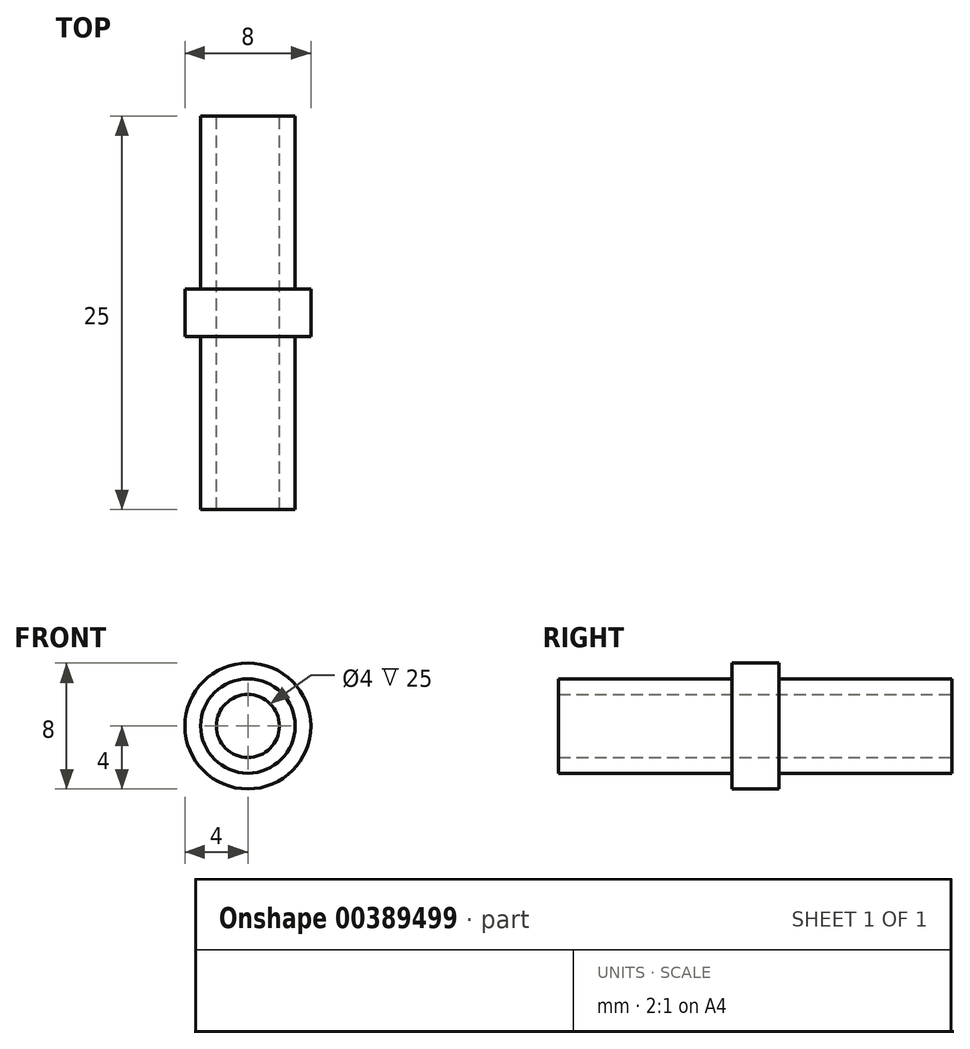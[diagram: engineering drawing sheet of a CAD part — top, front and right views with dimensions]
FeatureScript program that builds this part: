
annotation { "Feature Type Name" : "Feature", "Feature Type Description" : "" }
export const myFeature = defineFeature(function(context is Context, id is Id, definition is map)
    precondition{}
    {
        {
            var Q0;
            Q0=qCreatedBy(makeId("Front.planeOp"),FACE);
            var sketch = newSketch(context, id + "F0", { "sketchPlane" : qUnion([Q0])});
            skCircle(sketch, "E0", {"center": v(0, 0) * mm, "radius": 4 * mm});
            skSolve(sketch);
        }
        {
            var Q0;
            Q0=qCreatedBy(makeId("Front.planeOp"),FACE);
            var sketch = newSketch(context, id + "F1", { "sketchPlane" : qUnion([Q0])});
            skCircle(sketch, "E1", {"center": v(0, 0) * mm, "radius": 3 * mm});
            skSolve(sketch);
        }
        {
            var Q0;
            Q0=qSketchRegion(id+"F1",true);
            extrude(context, id + "F2", {"entities" : qUnion([Q0]), "depth" : 25 * mm});
        }
        {
            var Q0;
            Q0=qSketchRegion(id+"F0",true);
            extrude(context, id + "F3", {"entities" : qUnion([Q0]), "operationType" : NewBodyOperationType.ADD, "depth" : 14 * mm});
        }
        {
            var Q0;
            Q0=makeQuery(id+"F3.boolean.opBoolean","MERGE",FACE,{"derivedFrom":[makeQuery(id+"F2.opExtrude","CAP_FACE",FACE,{"disambiguationData":[OSD([sQuery(id+"F1.wireOp",EDGE,"E1")])],"isStart":true}),makeQuery(id+"F3.opExtrude","CAP_FACE",FACE,{"disambiguationData":[OSD([sQuery(id+"F0.wireOp",EDGE,"E0")])],"isStart":true})]});
            var sketch = newSketch(context, id + "F4", { "sketchPlane" : qUnion([Q0])});
            skCircle(sketch, "E2", {"center": v(0, 0) * mm, "radius": 3 * mm});
            skSolve(sketch);
        }
        {
            var Q0;
            Q0=makeQuery(id+"F4.imprint","IMPRINT",FACE,{"disambiguationData":[TD([[makeQuery(id+"F4.imprint","IMPRINT",EDGE,{"derivedFrom":sQuery(id+"F4.wireOp",EDGE,"E2")}),-1.0]])]});
            extrude(context, id + "F5", {"entities" : qUnion([Q0]), "operationType" : NewBodyOperationType.REMOVE, "oppositeDirection" : true, "depth" : 11 * mm});
        }
        {
            var Q0;
            Q0=makeQuery(id+"F3.boolean.opBoolean","MERGE",FACE,{"derivedFrom":[makeQuery(id+"F2.opExtrude","CAP_FACE",FACE,{"disambiguationData":[OSD([sQuery(id+"F1.wireOp",EDGE,"E1")])],"isStart":true}),makeQuery(id+"F3.opExtrude","CAP_FACE",FACE,{"disambiguationData":[OSD([sQuery(id+"F0.wireOp",EDGE,"E0")])],"isStart":true})]});
            var sketch = newSketch(context, id + "F6", { "sketchPlane" : qUnion([Q0])});
            skCircle(sketch, "E3", {"center": v(0, 0) * mm, "radius": 2 * mm});
            skSolve(sketch);
        }
        {
            var Q0;
            Q0=sQuery(id+"F6.wireOp",VERTEX,"E3.center");
            var Q1;
            Q1=makeQuery(id+"F2.opExtrude","SWEPT_BODY",BODY,{"disambiguationData":[OSD([sQuery(id+"F1.wireOp",EDGE,"E1")])]});
            hole(context, id + "F7", {"style" : HoleStyle.SIMPLE, "endStyle" : HoleEndStyle.THROUGH, "holeDiameter" : 4 * mm, "locations" : qUnion([Q0]), "scope" : qUnion([Q1]), "isTappedThrough" : true});
        }
    });
